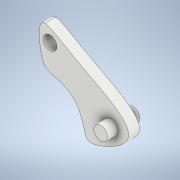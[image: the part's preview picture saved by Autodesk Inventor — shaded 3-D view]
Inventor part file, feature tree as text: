
AUTODESK INVENTOR PART (.ipt)
format: ipt  version: 2022 (Build 260153000, 153)  size: 130,560 bytes
history: native  units: in
note: dims shown in document units (in); Inventor stores cm internally (conversion verified against a paired STEP export)
features: extrude x3, sketch x2, projected_geometry x1
ambient origin geometry x8: Origin, YZ Plane, XZ Plane, XY Plane, X Axis, Y Axis, Z Axis, Center Point
bodies: Solid1 (feature_tree)
feature tree (6):
  sketch  "Sketch2"  dims[d0=0.1969in d1=0.0in d2=0.1969in d3=0.0in]
  extrude  "Extrusion1"  Depth=0.1969in TaperAngle=0.0deg
  extrude  "Extrusion2"  [1 undecoded]
  extrude  "Extrusion3"  [1 undecoded]
  sketch  "Sketch3"  dims[d4=0.1969in d5=0.0in]
  projected_geometry  "Projected Loop2"
note: 2 required parameter values undecoded (feature->parameter linkage not recoverable at this tier; creation-order binding heuristic only, values carry confidence <= 0.55)
